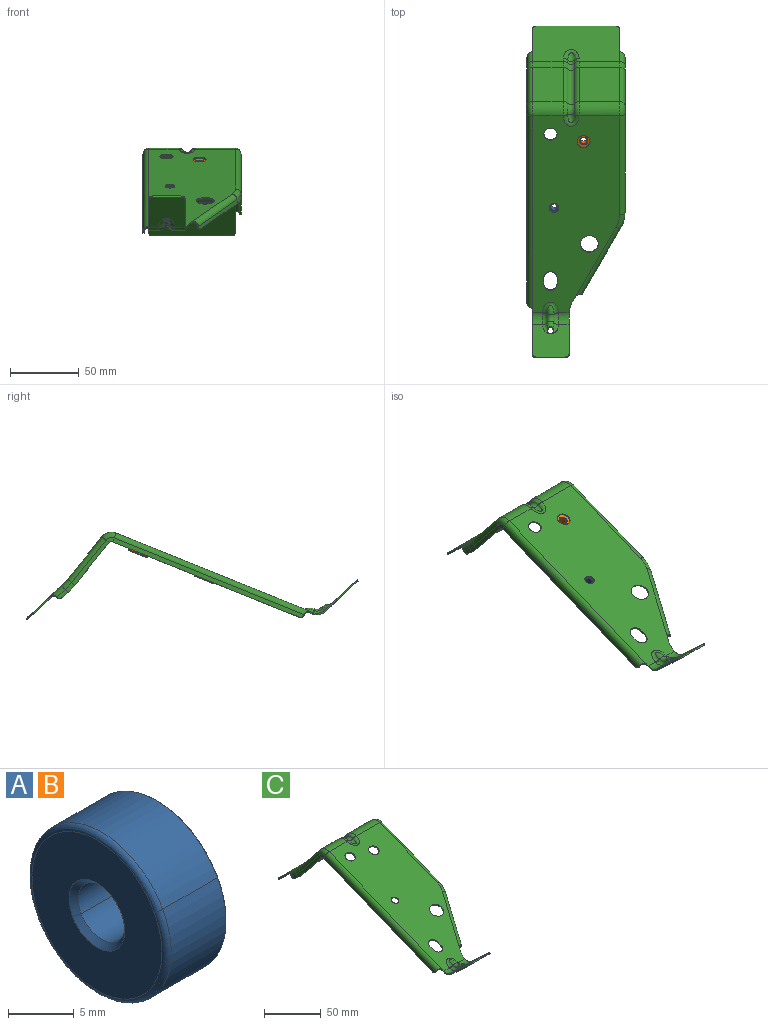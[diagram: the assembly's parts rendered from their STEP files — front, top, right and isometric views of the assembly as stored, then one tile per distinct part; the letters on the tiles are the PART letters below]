
ASSEMBLY  parts=3 mates=1
PART A: 14 faces, bbox 6.5x15x15 mm
  f0: revolved ~5.63x4.44mm, area 6.1mm2, adj f1,f3,f4
  f1: revolved ~5.63x4.44mm, area 6.1mm2, adj f0,f2,f4
  f2: cylinder r=2.5mm len=5.5mm, axis (1,0,0), area 43.2mm2, adj f1,f3,f6
  f3: cylinder r=2.5mm len=5.5mm, axis (1,0,0), area 43.2mm2, adj f0,f2,f7
  f4: plane 14.03x14.03mm, normal (-1,0,0), area 125.7mm2, adj f0,f1,f5,f8
  f5: revolved ~14.08x11.1mm, area 18.1mm2, adj f4,f8,f9
  f6: revolved ~5.63x4.44mm, area 6.1mm2, adj f2,f7,f10
  f7: revolved ~5.63x4.44mm, area 6.1mm2, adj f3,f6,f10
  f8: revolved ~14.08x11.1mm, area 18.1mm2, adj f4,f5,f11
  f9: cylinder r=7.5mm len=14.08mm, axis (-1,0,0), area 139mm2, adj f5,f11,f12
  f10: plane 14.83x14.83mm, normal (1,0,0), area 144.6mm2, adj f6,f7,f12,f13
  f11: cylinder r=7.5mm len=14.08mm, axis (-1,0,0), area 139mm2, adj f8,f9,f13
  f12: revolved ~14.08x11.1mm, area 3.3mm2, adj f9,f10,f13
  f13: revolved ~14.08x11.1mm, area 3.3mm2, adj f10,f11,f12
PART B: same geometry as A
PART C: 173 faces, bbox 77.1x244.8x67.9 mm
  f0: bspline ~3.89x1.27mm, area 4mm2, adj f1,f126,f127,f128
  f1: bspline ~1.98x1.2mm, area 1.9mm2, adj f0,f2,f124,f125
  f2: bspline ~11.49x8.45mm, area 65.4mm2, adj f1,f116,f119,f120,f124,f126,f128
  f3: bspline ~3.29x1.71mm, area 1.6mm2, adj f99,f111,f114,f115
  f4: bspline ~1.37x1.3mm, area 1.1mm2, adj f89,f100,f108,f113
  f5: bspline ~4.11x2.11mm, area 2.2mm2, adj f6,f106,f109,f110
  f6: bspline ~11.47x8.84mm, area 68.3mm2, adj f5,f97,f98,f106
  f7: bspline ~11.47x8.11mm, area 45.1mm2, adj f10,f58,f59,f98
  f8: bspline ~3.29x1.7mm, area 1.4mm2, adj f68,f71,f95,f96
  f9: bspline ~4.22x3.99mm, area 6.6mm2, adj f73,f87,f88,f168
  f10: bspline ~2.47x1.3mm, area 1mm2, adj f7,f43,f58,f77
  f11: bspline ~11.49x7.75mm, area 62.7mm2, adj f20,f21,f25,f34
  f12: bspline ~11.49x7.45mm, area 49.7mm2, adj f19,f26,f141,f148
  f13: bspline ~4.82x3.99mm, area 6.6mm2, adj f16,f17,f18,f149
  f14: cylinder r=3mm len=10.2mm, axis (0,-0.73,0.68), area 44.6mm2, adj f26,f28,f131,f132
  f15: plane 16.04x15.05mm, normal (-1,0,0), area 21mm2, adj f26,f34,f132,f133
  f16: plane 16.04x15.05mm, normal (1,0,0), area 21mm2, adj f13,f26,f34,f135
  f17: cylinder r=3mm len=10.2mm, axis (0,-0.73,0.68), area 44.6mm2, adj f13,f26,f136,f154
  f18: cylinder r=3mm len=4.27mm, axis (-1,-0.04,-0.04), area 4.7mm2, adj f13,f136,f139,f140
  f19: cylinder r=3mm len=2.98mm, axis (0,0.73,-0.68), area 8.3mm2, adj f12,f24,f26,f153
  f20: torus R=8mm, axis (-1,0,0), area 31.5mm2, adj f11,f142
  f21: cylinder r=4mm len=3.28mm, axis (0,-0.73,0.68), area 11.1mm2, adj f11,f31,f34,f142
  f22: cylinder r=4mm len=10.85mm, axis (0,-0.73,0.68), area 59.5mm2, adj f23,f32,f34,f132
  f23: plane 8.11x6.61mm, normal (-1,0.04,0.04), area 23mm2, adj f22,f129,f130,f145
  f24: cylinder r=4mm len=6.57mm, axis (0,-0.73,0.68), area 22.2mm2, adj f19,f141,f144,f148
  f25: cylinder r=4mm len=3.28mm, axis (0,0.73,-0.68), area 11.1mm2, adj f11,f34,f142,f157
  f26: plane 63x25.81mm, normal (0,-0.68,-0.73), area 2103.8mm2, adj f12,f14,f15,f16,f17,f19,f37,f133
  f27: torus R=49mm, axis (-1,0,0), area 18.7mm2, adj f37,f38,f141,f144
  f28: torus R=49mm, axis (-1,0,0), area 29.9mm2, adj f14,f37,f143,f164
  f29: plane 32.62x27.22mm, normal (1,-0.04,-0.03), area 118.6mm2, adj f143,f146,f164,f165
  f30: cylinder r=4mm len=31.81mm, axis (0,-0.63,0.78), area 304.5mm2, adj f35,f38,f144,f166
  f31: torus R=49mm, axis (-1,0,0), area 24.5mm2, adj f21,f40,f152,f172
  f32: torus R=49mm, axis (-1,0,0), area 39.3mm2, adj f22,f45,f145,f172
  f33: plane 32.62x27.22mm, normal (-1,0.04,0.03), area 118.6mm2, adj f45,f46,f145,f146
  f34: plane 63x25.81mm, normal (0,0.68,0.73), area 2103.8mm2, adj f11,f15,f16,f21,f22,f25,f42,f133
  f35: cylinder r=3mm len=31.54mm, axis (0,-0.63,0.78), area 114.2mm2, adj f30,f43,f44,f153
  f36: cylinder r=3mm len=32.52mm, axis (0,-0.63,0.78), area 180.1mm2, adj f44,f54,f154,f155
  f37: cylinder r=46mm len=22.26mm, axis (1,0,0), area 142.9mm2, adj f26,f27,f28,f56
  f38: cylinder r=3mm len=31.54mm, axis (0,0.63,-0.78), area 114.2mm2, adj f27,f30,f55,f56
  f39: cylinder r=3mm len=3.96mm, axis (-0.88,0.46,0.13), area 4.7mm2, adj f51,f61,f62,f169
  f40: cylinder r=4mm len=31.81mm, axis (0,0.63,-0.78), area 152.3mm2, adj f31,f65,f66,f161
  f41: cylinder r=4mm len=31.81mm, axis (0,-0.63,0.78), area 152.3mm2, adj f68,f69,f157,f161
  f42: cylinder r=45mm len=29.26mm, axis (1,0,0), area 183.8mm2, adj f34,f69,f157,f158
  f43: torus R=5mm, axis (1,0,0), area 26.6mm2, adj f10,f35,f77,f166
  f44: offset ~40.86x38.83mm, area 1156.9mm2, adj f35,f36,f77,f162
  f45: cylinder r=4mm len=33.12mm, axis (0,-0.63,0.78), area 240.2mm2, adj f32,f33,f66,f67
  f46: cone r=2.21mm half-angle=87deg, axis (1,0,0), area 14.2mm2, adj f33,f60,f67,f156
  f47: cylinder r=4mm len=33.12mm, axis (0,-0.63,0.78), area 240.2mm2, adj f69,f70,f158,f159
  f48: cone r=2.21mm half-angle=87deg, axis (-1,0,0), area 14.2mm2, adj f64,f70,f159,f160
  f49: torus R=9mm, axis (-1,0,0), area 45.3mm2, adj f65,f68,f71,f161
  f50: plane 139.11x57.62mm, normal (1,0.02,-0.05), area 444.5mm2, adj f73,f165,f167,f168
  f51: plane 48.84x28.02mm, normal (-0.88,0.46,0.13), area 173.9mm2, adj f39,f52,f74,f169
  f52: cone r=23mm half-angle=3deg, axis (0,0.37,-0.93), area 34.3mm2, adj f51,f53,f75,f170
  f53: plane 72.75x31.72mm, normal (-1,0.02,-0.05), area 231.8mm2, adj f52,f76,f163,f171
  f54: torus R=5mm, axis (-1,0,0), area 40.5mm2, adj f36,f76,f77,f163
  f55: torus R=5mm, axis (-1,0,0), area 26.6mm2, adj f38,f59,f78,f166
  f56: offset ~40.86x33.84mm, area 880.1mm2, adj f37,f38,f78,f164
  f57: torus R=5mm, axis (-1,0,0), area 40.5mm2, adj f73,f78,f164,f165
  f58: torus R=8mm, axis (-1,0,0), area 41.1mm2, adj f7,f10,f59,f166
  f59: bspline ~2.47x1.3mm, area 1mm2, adj f7,f55,f58,f78
  f60: plane 139.11x57.62mm, normal (-1,-0.02,0.05), area 444.5mm2, adj f46,f88,f167,f168
  f61: plane 48.84x28.02mm, normal (0.88,-0.46,-0.13), area 173.9mm2, adj f39,f63,f91,f169
  f62: bspline ~4.94x3.53mm, area 6.6mm2, adj f39,f74,f90,f91
  f63: cone r=23.99mm half-angle=3deg, axis (0,0.37,-0.93), area 35.8mm2, adj f61,f64,f92,f170
  f64: plane 72.75x31.72mm, normal (1,-0.02,0.05), area 231.8mm2, adj f48,f63,f93,f171
  f65: torus R=5mm, axis (-1,0,0), area 39.5mm2, adj f40,f49,f72,f94
  f66: offset ~38.86x31.84mm, area 880.1mm2, adj f40,f45,f94,f172
  f67: torus R=5mm, axis (-1,0,0), area 59.1mm2, adj f45,f46,f88,f94
  f68: torus R=5mm, axis (1,0,0), area 39.5mm2, adj f8,f41,f49,f95
  f69: offset ~38.86x36.83mm, area 1156.9mm2, adj f41,f42,f47,f95
  f70: torus R=5mm, axis (-1,0,0), area 59.1mm2, adj f47,f48,f93,f95
  f71: torus R=8mm, axis (-1,0,0), area 28.4mm2, adj f8,f49,f72,f96
  f72: bspline ~3.29x1.7mm, area 1.4mm2, adj f65,f71,f94,f96
  f73: cylinder r=3mm len=141.84mm, axis (0,-0.93,-0.37), area 684.8mm2, adj f9,f50,f57,f98
  f74: cylinder r=3mm len=50.85mm, axis (-0.48,-0.82,-0.33), area 273.8mm2, adj f51,f62,f75,f98
  f75: torus R=20mm, axis (0,0.37,-0.93), area 49.4mm2, adj f52,f74,f76,f98
  f76: cylinder r=3mm len=72.69mm, axis (0,-0.93,-0.37), area 351.9mm2, adj f53,f54,f75,f98
  f77: cylinder r=8mm len=29.26mm, axis (1,0,0), area 298.2mm2, adj f10,f43,f44,f54,f98
  f78: cylinder r=8mm len=22.26mm, axis (1,0,0), area 226.8mm2, adj f55,f56,f57,f59,f98
  f79: cylinder r=4.75mm len=9.5mm, axis (0,-0.37,0.93), area 29.8mm2, adj f98,f102
  f80: cylinder r=6.5mm len=13mm, axis (0,-0.37,0.93), area 40.8mm2, adj f98,f102
  f81: cylinder r=3.5mm len=7mm, axis (0,-0.37,0.93), area 22mm2, adj f98,f102
  f82: cylinder r=4.75mm len=9.5mm, axis (0,-0.37,0.93), area 14.9mm2, adj f83,f85,f98,f102
  f83: plane 5.01x2.8mm, normal (-1,0,0), area 5mm2, adj f82,f84,f98,f102
  f84: cylinder r=4.75mm len=9.5mm, axis (0,-0.37,0.93), area 14.9mm2, adj f83,f85,f98,f102
  f85: plane 5.01x2.8mm, normal (1,0,0), area 5mm2, adj f82,f84,f98,f102
  f86: cylinder r=4.75mm len=9.5mm, axis (0,-0.37,0.93), area 29.8mm2, adj f98,f102
  f87: plane 32.85x23.19mm, normal (-1,0,0), area 41mm2, adj f9,f98,f102,f105,f109,f114,f116,f117
  f88: cylinder r=4mm len=142.19mm, axis (0,-0.93,-0.37), area 913mm2, adj f9,f60,f67,f102
  f89: cylinder r=20mm len=8.24mm, axis (0,-0.37,0.93), area 8.9mm2, adj f4,f90,f98,f102
  f90: plane 4.45x2.57mm, normal (0.88,-0.44,-0.18), area 5mm2, adj f62,f89,f98,f102
  f91: cylinder r=4mm len=51.05mm, axis (-0.48,-0.82,-0.33), area 365mm2, adj f61,f62,f92,f102
  f92: torus R=20mm, axis (0,0.37,-0.93), area 67.7mm2, adj f63,f91,f93,f102
  f93: cylinder r=4mm len=73.05mm, axis (0,-0.93,-0.37), area 469.2mm2, adj f64,f70,f92,f102
  f94: cylinder r=9mm len=22.26mm, axis (1,0,0), area 255.2mm2, adj f65,f66,f67,f72,f102
  f95: cylinder r=9mm len=29.26mm, axis (1,0,0), area 335.5mm2, adj f8,f68,f69,f70,f102
  f96: bspline ~11.47x8.33mm, area 56.7mm2, adj f8,f71,f72,f102
  f97: bspline ~4.11x2.11mm, area 2.2mm2, adj f6,f106,f107,f108
  f98: plane 142.76x63.14mm, normal (0,0.37,-0.93), area 7733.4mm2, adj f6,f7,f73,f74,f75,f76,f77,f78
  f99: bspline ~11.47x8.63mm, area 57.8mm2, adj f3,f101,f102,f111
  f100: plane 29.89x23.19mm, normal (1,0,0), area 37.9mm2, adj f4,f103,f108,f113,f116,f117
  f101: bspline ~3.29x1.71mm, area 1.6mm2, adj f99,f111,f112,f113
  f102: plane 142.75x63.13mm, normal (0,-0.37,0.93), area 7733.4mm2, adj f79,f80,f81,f82,f83,f84,f85,f86
  f103: cylinder r=3mm len=3mm, axis (0,-0.68,-0.73), area 4.7mm2, adj f100,f104,f116,f117
  f104: plane 20.5x0.73mm, normal (0,-0.73,0.68), area 20.5mm2, adj f103,f105,f116,f117
  f105: cylinder r=3mm len=3mm, axis (0,-0.68,-0.73), area 4.7mm2, adj f87,f104,f116,f117
  f106: torus R=10mm, axis (1,0,0), area 18.8mm2, adj f5,f6,f97,f118
  f107: torus R=4mm, axis (1,0,0), area 42mm2, adj f97,f108,f118,f119
  f108: cylinder r=9mm len=9.51mm, axis (1,0,0), area 79.2mm2, adj f4,f97,f98,f100,f107,f116,f119
  f109: cylinder r=9mm len=9.51mm, axis (1,0,0), area 74.1mm2, adj f5,f87,f98,f110,f116,f120
  f110: torus R=4mm, axis (-1,0,0), area 42mm2, adj f5,f109,f118,f120
  f111: torus R=10mm, axis (1,0,0), area 30.3mm2, adj f3,f99,f101,f121
  f112: torus R=4mm, axis (1,0,0), area 30.1mm2, adj f101,f113,f121,f122
  f113: cylinder r=8mm len=8.45mm, axis (1,0,0), area 70.4mm2, adj f4,f100,f101,f102,f112,f117,f122
  f114: cylinder r=8mm len=8.45mm, axis (1,0,0), area 65.9mm2, adj f3,f87,f102,f115,f117,f123
  f115: torus R=4mm, axis (-1,0,0), area 30.1mm2, adj f3,f114,f121,f123
  f116: plane 26.5x23.68mm, normal (0,-0.68,-0.73), area 766.3mm2, adj f2,f87,f100,f103,f104,f105,f108,f109
  f117: plane 26.5x23.68mm, normal (0,0.68,0.73), area 766.3mm2, adj f87,f100,f103,f104,f105,f113,f114,f125
  f118: torus R=8mm, axis (-1,0,0), area 25.6mm2, adj f106,f107,f110,f126
  f119: cylinder r=5mm len=4.1mm, axis (0,0.73,-0.68), area 0.2mm2, adj f2,f107,f108,f126
  f120: cylinder r=5mm len=4.1mm, axis (0,-0.73,0.68), area 0.2mm2, adj f2,f109,f110,f126
  f121: torus R=8mm, axis (-1,0,0), area 33.2mm2, adj f111,f112,f115,f127
  f122: cylinder r=4mm len=3.28mm, axis (0,0.73,-0.68), area 0.1mm2, adj f112,f113,f125,f127
  f123: cylinder r=4mm len=3.28mm, axis (0,-0.73,0.68), area 0.1mm2, adj f114,f115,f125,f127
  f124: bspline ~5.01x2.8mm, area 8.1mm2, adj f1,f2,f125,f128
  f125: bspline ~11.49x8.19mm, area 54.1mm2, adj f1,f117,f122,f123,f124,f127,f128
  f126: torus R=10mm, axis (1,0,0), area 15.7mm2, adj f0,f2,f118,f119,f120
  f127: torus R=10mm, axis (1,0,0), area 25.3mm2, adj f0,f121,f122,f123,f125
  f128: bspline ~1.98x1.2mm, area 1.9mm2, adj f0,f2,f124,f125
  f129: cylinder r=3mm len=4.27mm, axis (-1,0.04,0.04), area 4.7mm2, adj f23,f130,f131,f132
  f130: plane 3.91x3.65mm, normal (-0.05,-0.68,-0.73), area 5.3mm2, adj f23,f129,f131,f147
  f131: plane 8.11x6.61mm, normal (1,-0.04,-0.04), area 23mm2, adj f14,f129,f130,f143
  f132: bspline ~4.82x3.99mm, area 6.6mm2, adj f14,f15,f22,f129
  f133: cylinder r=3mm len=3mm, axis (0,-0.68,-0.73), area 4.7mm2, adj f15,f26,f34,f134
  f134: plane 57x0.73mm, normal (0,0.73,-0.68), area 57mm2, adj f26,f34,f133,f135
  f135: cylinder r=3mm len=3mm, axis (0,-0.68,-0.73), area 4.7mm2, adj f16,f26,f34,f134
  f136: plane 8.11x6.61mm, normal (-1,-0.04,-0.04), area 23mm2, adj f17,f18,f137,f139
  f137: cone r=48.84mm half-angle=87deg, axis (1,0,0), area 21.1mm2, adj f136,f138,f154,f155
  f138: cone r=52.34mm half-angle=3deg, axis (-1,0,0), area 7.2mm2, adj f137,f139,f150,f151
  f139: plane 3.91x3.65mm, normal (0.05,-0.68,-0.73), area 5.3mm2, adj f18,f136,f138,f140
  f140: plane 8.11x6.61mm, normal (1,0.04,0.04), area 23mm2, adj f18,f139,f149,f150
  f141: cylinder r=3mm len=2.98mm, axis (0,-0.73,0.68), area 8.3mm2, adj f12,f24,f26,f27
  f142: cylinder r=3mm len=4.92mm, axis (0,-0.73,0.68), area 16.6mm2, adj f20,f21,f25,f152
  f143: cone r=48.84mm half-angle=87deg, axis (-1,0,0), area 21.1mm2, adj f28,f29,f131,f147
  f144: torus R=45mm, axis (-1,0,0), area 52mm2, adj f24,f27,f30,f153
  f145: cone r=48.79mm half-angle=87deg, axis (-1,0,0), area 21.1mm2, adj f23,f32,f33,f147
  f146: plane 30.77x24.93mm, normal (-0.05,-0.78,-0.63), area 39.5mm2, adj f29,f33,f147,f156
  f147: cone r=52.34mm half-angle=3deg, axis (1,0,0), area 7.2mm2, adj f130,f143,f145,f146
  f148: torus R=8mm, axis (-1,0,0), area 45.6mm2, adj f12,f24
  f149: cylinder r=4mm len=10.85mm, axis (0,-0.73,0.68), area 59.5mm2, adj f13,f34,f140,f158
  f150: cone r=48.79mm half-angle=87deg, axis (1,0,0), area 21.1mm2, adj f138,f140,f158,f159
  f151: plane 30.77x24.93mm, normal (0.05,-0.78,-0.63), area 39.5mm2, adj f138,f155,f159,f160
  f152: torus R=45mm, axis (-1,0,0), area 38.3mm2, adj f31,f142,f157,f161
  f153: torus R=49mm, axis (1,0,0), area 18.7mm2, adj f19,f35,f144,f162
  f154: torus R=49mm, axis (-1,0,0), area 29.9mm2, adj f17,f36,f137,f162
  f155: plane 32.62x27.22mm, normal (-1,-0.04,-0.03), area 118.6mm2, adj f36,f137,f151,f163
  f156: cone r=2.19mm half-angle=3deg, axis (-1,0,0), area 2.8mm2, adj f46,f146,f165,f167
  f157: torus R=49mm, axis (1,0,0), area 24.5mm2, adj f25,f41,f42,f152
  f158: torus R=49mm, axis (-1,0,0), area 39.3mm2, adj f42,f47,f149,f150
  f159: plane 32.62x27.22mm, normal (1,0.04,0.03), area 118.6mm2, adj f47,f48,f150,f151
  f160: cone r=2.19mm half-angle=3deg, axis (1,0,0), area 2.8mm2, adj f48,f151,f163,f171
  f161: cylinder r=3mm len=31.54mm, axis (0,-0.63,0.78), area 228.4mm2, adj f40,f41,f49,f152
  f162: cylinder r=46mm len=29.26mm, axis (1,0,0), area 187.9mm2, adj f26,f44,f153,f154
  f163: cone r=2.16mm half-angle=87deg, axis (-1,0,0), area 14mm2, adj f53,f54,f155,f160
  f164: cylinder r=3mm len=32.52mm, axis (0,-0.63,0.78), area 180.1mm2, adj f28,f29,f56,f57
  f165: cone r=2.16mm half-angle=87deg, axis (1,0,0), area 14mm2, adj f29,f50,f57,f156
  f166: torus R=9mm, axis (-1,0,0), area 52.5mm2, adj f30,f43,f55,f58
  f167: plane 135.23x54.68mm, normal (-0.05,0.37,-0.93), area 145.8mm2, adj f50,f60,f156,f168
  f168: cylinder r=3mm len=3.92mm, axis (-1,-0.02,0.05), area 4.7mm2, adj f9,f50,f60,f167
  f169: plane 45.8x27.33mm, normal (0.05,0.35,-0.94), area 55.6mm2, adj f39,f51,f61,f170
  f170: cone r=998.63mm half-angle=87deg, axis (0,-0.37,0.93), area 11.7mm2, adj f52,f63,f169,f171
  f171: plane 71.65x28.99mm, normal (0.05,0.37,-0.93), area 77.3mm2, adj f53,f64,f160,f170
  f172: cylinder r=45mm len=22.26mm, axis (1,0,0), area 139.8mm2, adj f31,f32,f34,f66
PLACE A rot(axis=(0.19,0.96,0.19),92.1deg) t=(11.24,-189.62,-294.03)mm
PLACE B rot(axis=(0.19,-0.96,-0.19),92.1deg) t=(32.57,-143.95,-269.23)mm
PLACE C t=(27.07,-61.53,-322.28)mm
MATE cylindrical A.f9 <-> C.f81  axis (0,0.37,-0.93) through (11.24,-189.62,-294.03)mm
